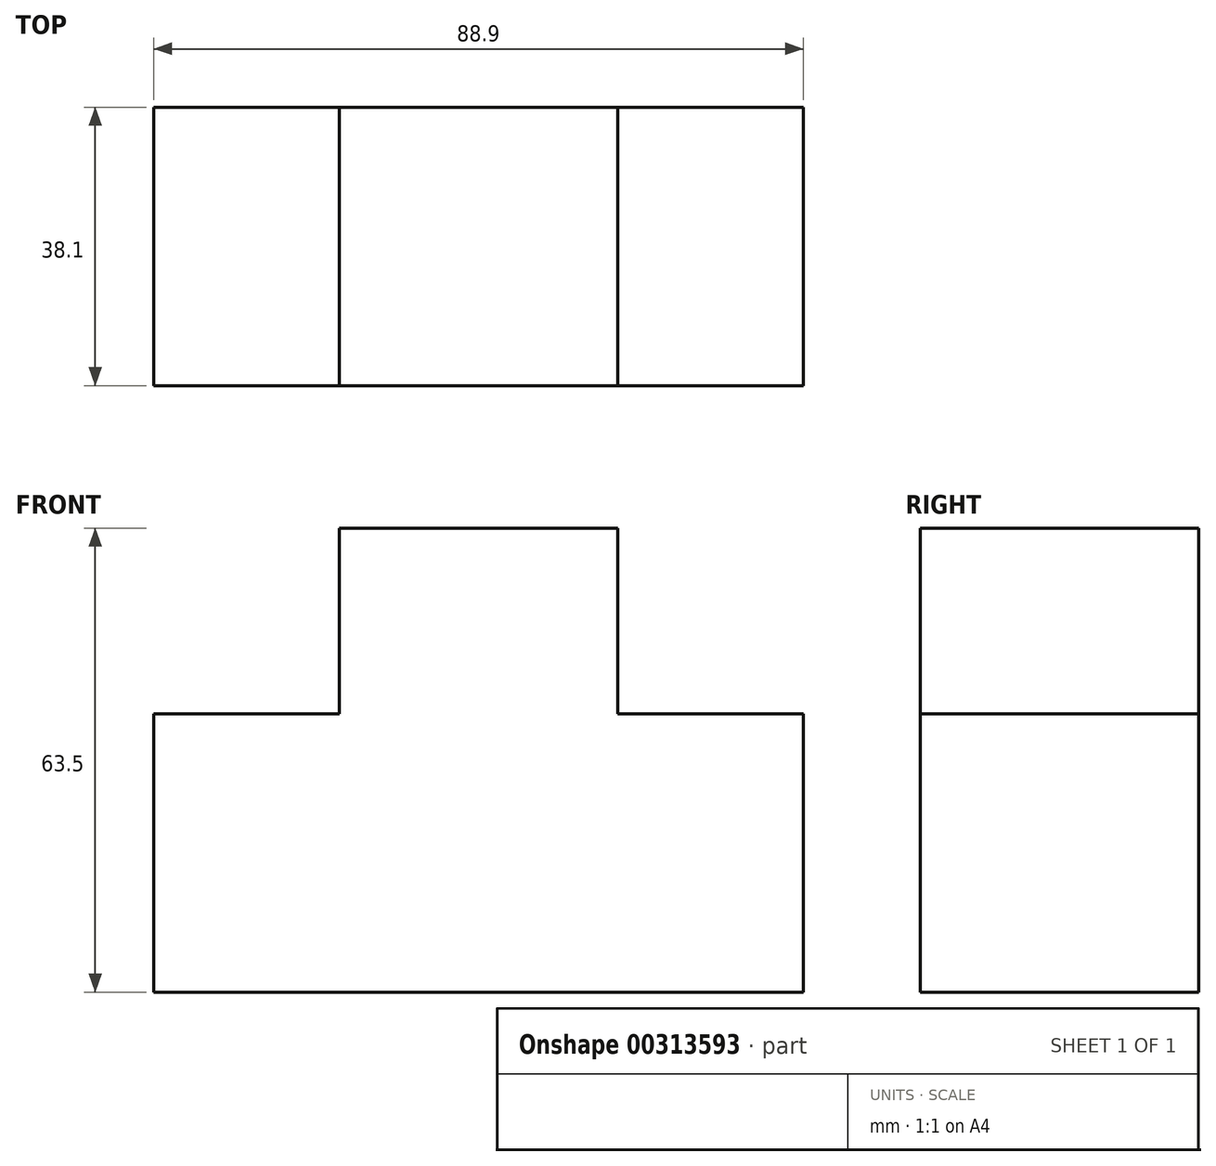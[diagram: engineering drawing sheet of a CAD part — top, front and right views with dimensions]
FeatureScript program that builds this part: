
annotation { "Feature Type Name" : "Feature", "Feature Type Description" : "" }
export const myFeature = defineFeature(function(context is Context, id is Id, definition is map)
    precondition{}
    {
        {
            var Q0;
            Q0=qCreatedBy(makeId("Front.planeOp"),FACE);
            var sketch = newSketch(context, id + "F0", { "sketchPlane" : qUnion([Q0])});
            skLineSegment(sketch, "E0", {"start": v(-42.2, -66.03) * mm, "end": v(46.7, -66.03) * mm});
            skLineSegment(sketch, "E1", {"start": v(46.7, -66.03) * mm, "end": v(46.7, -27.93) * mm});
            skLineSegment(sketch, "E2", {"start": v(46.7, -27.93) * mm, "end": v(21.3, -27.93) * mm});
            skLineSegment(sketch, "E3", {"start": v(21.3, -27.93) * mm, "end": v(21.3, -2.53) * mm});
            skLineSegment(sketch, "E4", {"start": v(21.3, -2.53) * mm, "end": v(-16.8, -2.53) * mm});
            skLineSegment(sketch, "E5", {"start": v(-16.8, -2.53) * mm, "end": v(-16.8, -27.93) * mm});
            skLineSegment(sketch, "E6", {"start": v(-16.8, -27.93) * mm, "end": v(-42.2, -27.93) * mm});
            skLineSegment(sketch, "E7", {"start": v(-42.2, -27.93) * mm, "end": v(-42.2, -66.03) * mm});
            skSolve(sketch);
        }
        {
            var Q0;
            Q0=makeQuery(id+"F0.imprint","IMPRINT",FACE,{"disambiguationData":[TD([[makeQuery(id+"F0.imprint","IMPRINT",EDGE,{"derivedFrom":sQuery(id+"F0.wireOp",EDGE,"E0")}),1.0]])]});
            extrude(context, id + "F1", {"entities" : qUnion([Q0]), "depth" : 38.1 * mm});
        }
    });
